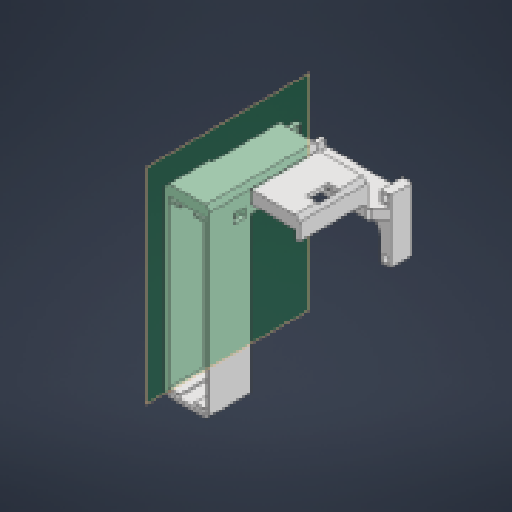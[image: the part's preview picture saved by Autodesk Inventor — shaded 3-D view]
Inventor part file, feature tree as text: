
AUTODESK INVENTOR PART (.ipt)
format: ipt  version: 2024.1 (Build 281209000, 209)  size: 512,000 bytes
history: native  units: in
note: dims shown in document units (in); Inventor stores cm internally (conversion verified against a paired STEP export)
features: reference x18, extrude x16, sketch x11, projected_geometry x10, other x9, chamfer x4, fillet x2, plane x1
ambient origin geometry x8: Origin, YZ Plane, XZ Plane, XY Plane, X Axis, Y Axis, Z Axis, Center Point
bodies: Solid1 (feature_tree)
feature tree (71):
  sketch  "Sketch1"  dims[d0=0.002in d1=0.1254in]
  extrude  "Extrusion1"  Depth=0.1254in
  extrude  "Extrusion2"  Depth=0.25in TaperAngle=0.0deg
  plane  "Work Plane1"
  sketch  "Sketch2"  dims[d2=0.015in d3=0.25in d4=0.0in]
  extrude  "Extrusion3"  Depth=0.429in
  extrude  "Extrusion4"  Depth=0.005in
  extrude  "Extrusion5"  Depth=0.0625in
  extrude  "Extrusion6"  Depth=0.15in
  extrude  "Extrusion7"  Depth=0.0625in TaperAngle=0.0deg
  extrude  "Extrusion8"  Depth=0.05in TaperAngle=0.0deg
  sketch  "Sketch5"  dims[d10=0.002in d11=0.0625in]
  extrude  "Extrusion9"  Depth=0.025in
  extrude  "Extrusion10"  Depth=0.175in
  extrude  "Extrusion11"  Depth=0.025in
  extrude  "Extrusion12"  Depth=0.175in
  chamfer  "Chamfer1"  Distance=0.0125in
  fillet  "Fillet2"  Radius=0.1in
  chamfer  "Chamfer2"  Distance=0.05in
  extrude  "Extrusion13"  Depth=0.05in
  fillet  "Fillet3"  Radius=0.05in
  extrude  "Extrusion14"  Depth=0.125in TaperAngle=0.0deg
  chamfer  "Chamfer3"  Distance=0.05in
  extrude  "Extrusion15"  TaperAngle=0.0deg  [1 undecoded]
  extrude  "Extrusion16"  Depth=0.2in
  chamfer  "Chamfer4"  Distance=0.1in
  reference  "Reference1"
  reference  "Reference2"
  reference  "Reference3"
  reference  "Reference4"
  reference  "Reference5"
  reference  "Reference6"
  projected_geometry  "Projected Loop1"
  reference  "Reference7"
  reference  "Reference8"
  reference  "Reference9"
  reference  "Reference10"
  reference  "Reference11"
  reference  "Reference12"
  sketch  "Sketch3"  dims[d5=0.429in d6=0.0in d7=0.002in]
  projected_geometry  "Projected Loop2"
  sketch  "Sketch4"  dims[d8=0.0in d9=0.005in]
  projected_geometry  "Projected Loop3"
  projected_geometry  "Projected Loop4"
  reference  "Reference13"
  sketch  "Sketch6"  dims[d12=0.067in d13=0.15in]
  projected_geometry  "Projected Loop5"
  sketch  "Sketch7"  dims[d14=0.0625in d15=0.0in d16=0.459in d17=0.0in]
  reference  "Reference14"
  reference  "Reference15"
  projected_geometry  "Projected Loop6"
  sketch  "Sketch8"  dims[d18=0.488in d19=0.0in d20=0.05in d21=0.0in]
  projected_geometry  "Projected Loop7"
  projected_geometry  "Projected Loop8"
  sketch  "Sketch9"  dims[d22=0.0125in d23=0.0in d24=0.025in]
  reference  "Reference16"
  reference  "Reference17"
  sketch  "Sketch10"  dims[d25=0.025in d26=0.175in]
  reference  "Reference18"
  sketch  "Sketch11"  dims[d27=0.025in d28=0.025in d29=0.175in d30=0.0125in d31=0.0in d32=0.1in d33=0.05in d35=0.05in d36=0.05in d37=1.0in d38=0.0in d39=0.05in d40=0.0in d41=0.0in d42=0.0in d43=0.2in d44=0.1in d45=0.0in d47=0.05in d48=0.125in d49=45.0deg d50=0.25in d51=0.112in d52=0.125in d53=45.0deg d54=0.1388in d55=0.0in d56=0.025in d57=0.35in d58=0.0in d59=0.01in d60=0.125in d61=45.0deg d62=0.005in d63=0.05in d64=0.1in d65=0.05in d66=0.1in d67=0.14in d68=0.0in d69=0.015in d70=0.015in d71=0.03in d72=0.0in d73=0.02in d74=0.125in d75=45.0deg]
  projected_geometry  "Projected Loop9"
  projected_geometry  "Projected Loop10"
  other  "<userpath>\Documents\School\FallCAD\Bio\Bio.iam"
  other  "Bio.iam"
  other  "arduino nano:1"
  other  "Servo HS425BB:1"
  other  "CUI_DEVICES_TS04-66-50-BK-160-SMT:1"
  other  "CUI_DEVICES_TS04-66-50-BK-160-SMT_2:1"
  other  "AAA Battery:1"
  other  "CUI_DEVICES_TS04-66-50-BK-160-SMT_1:1"
  other  "Leg_MIR:1"
note: 1 required parameter value undecoded (feature->parameter linkage not recoverable at this tier; creation-order binding heuristic only, values carry confidence <= 0.55)
